# Revit family: CM20318 Vitocrossal 200 CM2 620 575kW
name_source: partatom
category: Equipos mecánicos
revit_build: Autodesk Revit 2017 (Build: 20160225_1515(x64)
units: mm (PartAtom-declared; Revit-internal decimal feet)

## family parameters
Compartido = No
Corte con vacíos al cargar = No
Cota de conector redondo = Diámetro de uso
Número OmniClass = 23.75.00.00
Punto de cálculo de habitación = No
Se basa en plano de trabajo = No
Siempre vertical = Sí
Tipo de pieza = Normal
Título OmniClass = Climate Control (HVAC)

## types (1)
- Standard
    Descripción = Vitocrossal 200 CM2 620/575kW
Vitotronic 100 GC4B
VIESSMANN Vitocrossal 200, Typ CM2
Gas-Brennwertkessel mit MatriX-
Zylinderbrenner.

Nach EN 303, EN 483, EN 677, EN 12828,
EN 15417 und EN 15420, mit
CE-Kennzeichnung.
Für geschlossene Heizungsanlagen mit
zul. Vorlauftemperaturen (=Absicherungs-
temperaturen) bis 110 Grad C. Für den
besonders energiesparenden Betrieb mit
gleitend abgesenkter
Kesselwassertemperatur mit
Brennwertnutzung. Für die Verbrennung
von Gas nach DVGW- Arbeitsblatt G 260.
Sehr leiser Betrieb und niedrige
Schadstoff-Emissionen durch
modulierenden MatriX-Zylinderbrenner.
Kompakter Brennwertkessel mit Edel-
stahl-Brennraum als Durchgangsbrennraum
mit niedriger Brennraumbelastung,
dadurch schadstoffarme Verbrennung mit
niedrigen Stickoxid-Emissionen. Mit
Inox-Crossal-Heizflächen aus Edelstahl,
für hochwirksame Brennwertnutzung und
hohe Betriebssicherheit. Heiz- und
abgasberührten Teile aus Edelstahl
1.4571, Abgassammelkasten mit
Abgasanschluss aus Kunststoff (PP).
Brennwertoptimierte Ausführung im
Gegenstromprinzip von Kesselwasser und
Heizgas. Heizkessel mit großem
Wasserinhalt. Verstärkter
Selbstreinigungseffekt durch Gleichstrom
von Heizgas und Kondenswasser und
glatter Edelstahloberfläche.
Kesselkörper allseitig mit starker
Verbundwärmedämmung (80 mm) versehen.
Leichte und zeitsparende Montage der
Kesselverkleidung mit VIESSMANN Fastfix-
Montagesystem.

Mit Kesselkreisregelung Vitotronic 100,
Typ GC4B für den Betrieb mit angehobener
Kesselwassertemperatur oder
witterungsgeführten Betrieb in
Verbindung mit einer externen Regelung.
Für den Betrieb mit zweistufigen oder
modulierenden Brennern. Beimischpumpe
oder stetige Rücklauftemperaturregelung
(alternativ zum Speicherladesystem mit
geregeltem 3-Wege-Ventil) sind möglich
(jeweils nach Kessel und
Anlagenausführung). Einfache
Inbetriebnahme durch Plug and
Work-Funktion. Mit adaptiver
Speichertemperaturregelung (alternativ
Regelung eines Speicherladesystems mit
geregeltem 3-Wege-Ventil), integriertem
Diagnosesystem, Sommersparschaltung und
Pumpenblockierschutz. Busverbindung zum
Feuerungsautomaten. Externe Geräte
werden über Rast 5-Systemstecker
angeschlossen.
Die Vitotronic 100 enthält:
Anlagenschalter,
Schornsteinfeger-Prüfschalter,
elektronischen
Maximaltemperaturbegrenzer, Betriebs-
und Störanzeige, Optolink
Laptop-Schnittstelle und Bedienteil.
Einfache Bedienung mittels grafischem
Display mit Piktogrammen und
kontrastreicher
schwarz/weiß-Darstellung. Möglichkeiten
zur Einstellung von Betriebsprogramm und
Sollwerten sowie zur Abfrage von
Temperaturen. Mit Anschlussmöglichkeit
für externes Anfordern, Kesselfreigabe
und Einschalten der Brennerstufen.
Kommunikationsfähig über KM-BUS und
LON-BUS (durch Einbau des
Kommunikationsmodul LON, Zubehör). Über
KM-BUS ist eine einfache Fernüberwachung
möglich (Vitocom 100 als Zubehör
erforderlich). Über LON-BUS ist die
Fernüberwachung und -bedienung der
Heizungsanlage mit Vitocom 200 (Zubehör)
und Vitodata 100 (Zubehör) möglich. In
Verbindung mit Vitocom 300 (Zubehör) und
Vitodata 300 (Zubehör) ist zusätzlich
die Fernparametrierung möglich. Zugriff
auf Vitodata über PC mit Webbrowser und
Internet. Über LON-BUS und/oder Vitogate
200, Typ EIB (Zubehör)
kommunikationsfähig mit übergeordneten
Leitsystemen. Datenaustausch mit bis zu
32 Heizkreisregelungen Vitotronic 200-H
über LON- BUS ist möglich. Für die
Vorgabe des
Kesselwassertemperatur-Sollwerts über 0
-10 V-Eingang, externes Sperren mit
Sammelstörmeldung, Störungsmeldungen und
Ansteuerung Zubringerpumpe zu einer
Unterstation ist eine
Funktionserweiterung der Regelung mit
der Erweiterung EA1 (Zubehör)
erforderlich. Anschluss zusätzlicher
externer Sicherheitseinrichtungen (z.B.
Wassermangelsicherung, Druckbegrenzer
etc.) ist über einen Steckadapter für
externe Sicherheitseinrichtungen
(Zubehör) möglich.
Mit MatriX-Zylinderbrenner zur
Verbrennung von Erdgas E und LL sowie
Flüssiggas P nach EN 437.
Modulierender Brenner
(Modulationsbereich 1:5) mit
Gaskombiregler. Gaskombiregler mit zwei
Gasmagnetventilen (davon ein
Sicherheitsmagnetventil),
Gasdruckwächter und
Ventil-Dichtheitskontrollsystem. Mit
Kesseltemperatursensor, elektronischem
Temperaturregler und
Sicherheitstemperaturbegrenzer im
Feuerungsautomat entsprechend EN 12828.
Mit Doppelsensor zur
Abgastemperaturbegrenzung und
BUS-Verbindung zur Kesselkreisregelung.
Der Brenner ist auf die
Nenn-Wärmeleistung des Heizkessels
einreguliert und warm geprüft. Für
raumluftabhängigen oder
raumluftunabhängigen Betrieb. Für
Gasanschlussdruck 20 mbar.
Lieferumfang:
Heizkessel mit MatriX-Zylinderbrenner,
Gegenflansche mit Schrauben und
Dichtungen, Wärmedämmung,
Geruchsverschluss (Siphon) und
Kesselkreisregelung.

Nenn-Wärmeleistung bei:
- Heizbetrieb 50/30 Grad C:      620 kW
- Heizbetrieb 80/60 Grad C:      575 kW
Abmessungen:
- Länge:                       2.525 mm
- Breite:                      1.295 mm
- Höhe:                        1.580 mm
- Gewicht:                       758 kg
Inhalt Kesselwasser:             503 l
Zul. Betriebsdruck:                6 bar
Abgasanschluss:                  250 mm
Norm-Nutzungsgrad (Hs) bis:      98% %
Norm-Nutzungsgrad (Hi) bis:     109% %
Technische Daten zur Bestimmung der
Energieeffizienzklasse (ErP-Label):
Temperaturregler:
- Temperaturregler Klasse:           I
- Beitrag Raumheizungs-Energieeffizienz:
                                     1 %

Bestell-Nr.: CM20318
    Fabricante = Viessmann
    Modelo = CM20318

## geometry (parser evidence)
native form markers: Sweep x2
no freeform markers — native parametric forms only
